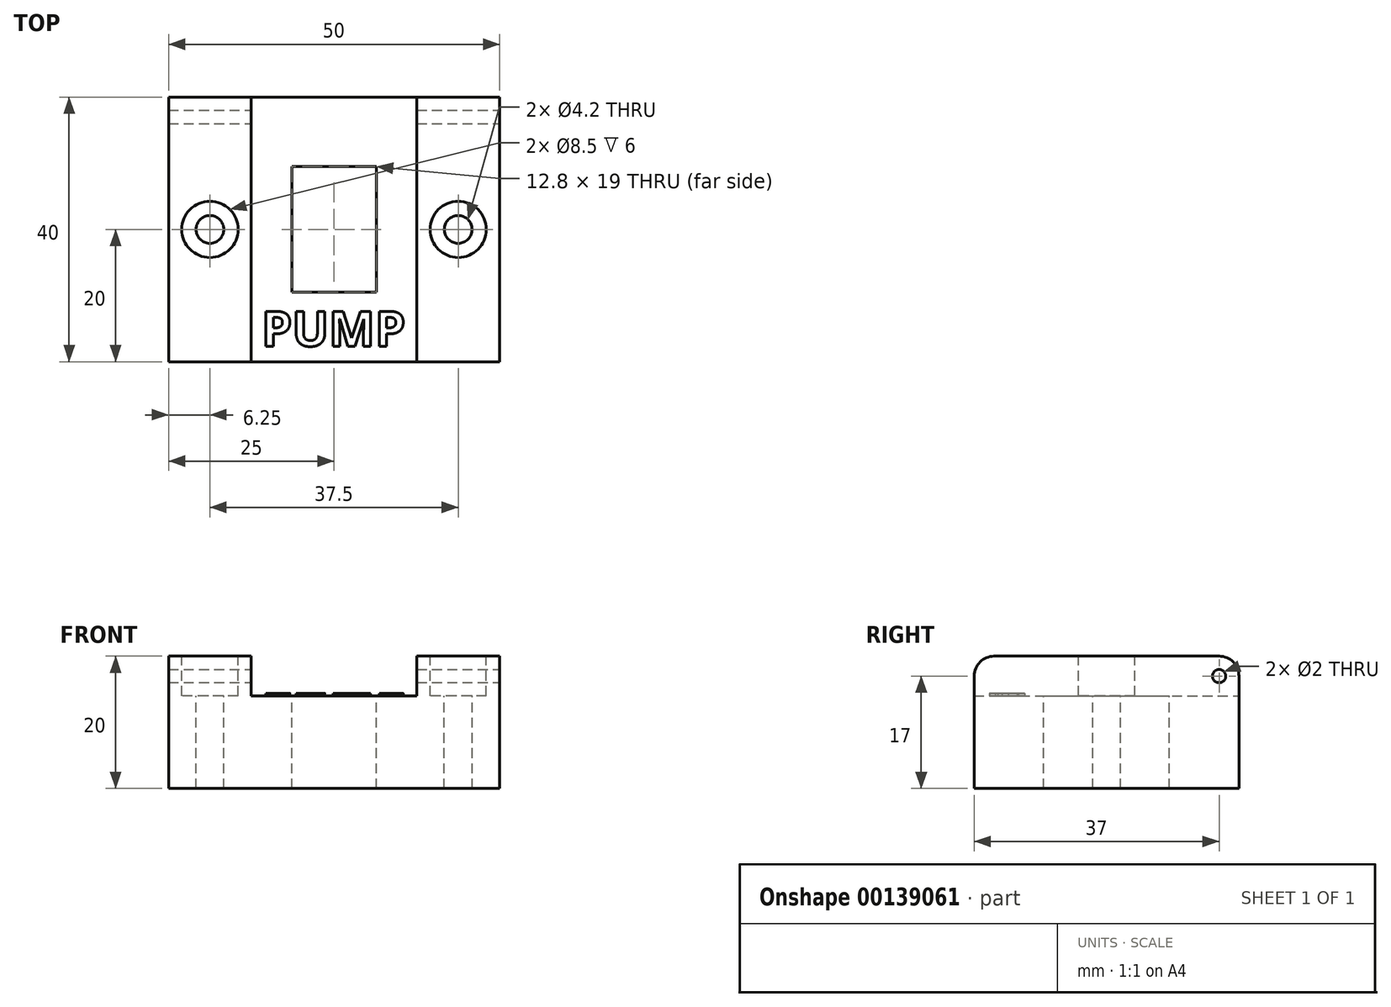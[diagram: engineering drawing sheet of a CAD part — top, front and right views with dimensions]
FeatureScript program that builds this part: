
annotation { "Feature Type Name" : "Feature", "Feature Type Description" : "" }
export const myFeature = defineFeature(function(context is Context, id is Id, definition is map)
    precondition{}
    {
        {
            var Q0;
            Q0=qCreatedBy(makeId("Top.planeOp"),FACE);
            var sketch = newSketch(context, id + "F0", { "sketchPlane" : qUnion([Q0])});
            skLineSegment(sketch, "E0.bottom", {"start": v(25, -20) * mm, "end": v(-25, -20) * mm});
            skLineSegment(sketch, "E0.top", {"start": v(25, 20) * mm, "end": v(-25, 20) * mm});
            skLineSegment(sketch, "E0.left", {"start": v(25, -20) * mm, "end": v(25, 20) * mm});
            skLineSegment(sketch, "E0.right", {"start": v(-25, -20) * mm, "end": v(-25, 20) * mm});
            skPoint(sketch, "E0.middle", {"position": v(0, 0) * mm});
            skSolve(sketch);
        }
        {
            var Q0;
            Q0=makeQuery(id+"F0.imprint","IMPRINT",FACE,{"disambiguationData":[TD([[makeQuery(id+"F0.imprint","IMPRINT",EDGE,{"derivedFrom":sQuery(id+"F0.wireOp",EDGE,"E0.bottom")}),-1.0]])]});
            extrude(context, id + "F1", {"entities" : qUnion([Q0]), "depth" : 14 * mm});
        }
        {
            var Q0;
            Q0=makeQuery(id+"F1.opExtrude","CAP_FACE",FACE,{"disambiguationData":[OSD([sQuery(id+"F0.wireOp",EDGE,"E0.bottom"),sQuery(id+"F0.wireOp",EDGE,"E0.top"),sQuery(id+"F0.wireOp",EDGE,"E0.left"),sQuery(id+"F0.wireOp",EDGE,"E0.right")])],"isStart":false});
            var sketch = newSketch(context, id + "F2", { "sketchPlane" : qUnion([Q0])});
            skLineSegment(sketch, "E1.bottom", {"start": v(6.4, -9.5) * mm, "end": v(-6.4, -9.5) * mm});
            skLineSegment(sketch, "E1.top", {"start": v(6.4, 9.5) * mm, "end": v(-6.4, 9.5) * mm});
            skLineSegment(sketch, "E1.left", {"start": v(6.4, -9.5) * mm, "end": v(6.4, 9.5) * mm});
            skLineSegment(sketch, "E1.right", {"start": v(-6.4, -9.5) * mm, "end": v(-6.4, 9.5) * mm});
            skPoint(sketch, "E1.middle", {"position": v(0, 0) * mm});
            skSolve(sketch);
        }
        {
            var Q0;
            Q0 = qSketchRegion(id + "F2", true);
            extrude(context, id + "F3", {"entities" : qUnion([Q0]), "operationType" : NewBodyOperationType.REMOVE, "endBound" : BoundingType.UP_TO_NEXT, "oppositeDirection" : true, "depth" : 25 * mm});
        }
        {
            var Q0;
            Q0=makeQuery(id+"F1.opExtrude","CAP_FACE",FACE,{"disambiguationData":[OSD([sQuery(id+"F0.wireOp",EDGE,"E0.bottom"),sQuery(id+"F0.wireOp",EDGE,"E0.top"),sQuery(id+"F0.wireOp",EDGE,"E0.left"),sQuery(id+"F0.wireOp",EDGE,"E0.right")])],"isStart":false});
            var sketch = newSketch(context, id + "F4", { "sketchPlane" : qUnion([Q0])});
            skLineSegment(sketch, "E2.bottom", {"start": v(25, -20) * mm, "end": v(-25, -20) * mm});
            skLineSegment(sketch, "E2.top", {"start": v(25, 20) * mm, "end": v(-25, 20) * mm});
            skLineSegment(sketch, "E2.left", {"start": v(25, -20) * mm, "end": v(25, 20) * mm});
            skLineSegment(sketch, "E2.right", {"start": v(-25, -20) * mm, "end": v(-25, 20) * mm});
            skPoint(sketch, "E2.middle", {"position": v(0, 0) * mm});
            skLineSegment(sketch, "E3.bottom", {"start": v(12.5, -20) * mm, "end": v(-12.5, -20) * mm});
            skLineSegment(sketch, "E3.top", {"start": v(12.5, 20) * mm, "end": v(-12.5, 20) * mm});
            skLineSegment(sketch, "E3.left", {"start": v(12.5, -20) * mm, "end": v(12.5, 20) * mm});
            skLineSegment(sketch, "E3.right", {"start": v(-12.5, -20) * mm, "end": v(-12.5, 20) * mm});
            skSolve(sketch);
        }
        {
            var Q0;
            {var subQ0=sQuery(id+"F4.wireOp",EDGE,"E2.right");Q0=makeQuery(id+"F4.imprint","IMPRINT",FACE,{"disambiguationData":[TD([[makeQuery(id+"F4.imprint","IMPRINT",EDGE,{"derivedFrom":subQ0}),-1.0]])]});}
            var Q1;
            {var subQ0=sQuery(id+"F4.wireOp",EDGE,"E2.left");Q1=makeQuery(id+"F4.imprint","IMPRINT",FACE,{"disambiguationData":[TD([[makeQuery(id+"F4.imprint","IMPRINT",EDGE,{"derivedFrom":subQ0}),1.0]])]});}
            extrude(context, id + "F5", {"entities" : qUnion([Q0, Q1]), "operationType" : NewBodyOperationType.ADD, "depth" : 6 * mm});
        }
        {
            var Q0;
            Q0=makeQuery(id+"F5.opExtrude","CAP_FACE",FACE,{"disambiguationData":[OSD([sQuery(id+"F4.wireOp",EDGE,"E2.bottom"),sQuery(id+"F4.wireOp",EDGE,"E2.top"),sQuery(id+"F4.wireOp",EDGE,"E2.left"),sQuery(id+"F4.wireOp",EDGE,"E3.left")])],"isStart":false});
            var sketch = newSketch(context, id + "F6", { "sketchPlane" : qUnion([Q0])});
            skLineSegment(sketch, "E4", {"start": v(-25.03, 0) * mm, "end": v(25, 0) * mm, "construction": true});
            skCircle(sketch, "E5", {"center": v(-18.75, 0) * mm, "radius": 2.1 * mm});
            skCircle(sketch, "E6", {"center": v(18.75, 0) * mm, "radius": 2.1 * mm});
            skSolve(sketch);
        }
        {
            var Q0;
            Q0=makeQuery(id+"F6.imprint","IMPRINT",FACE,{"disambiguationData":[TD([[makeQuery(id+"F6.imprint","IMPRINT",EDGE,{"derivedFrom":sQuery(id+"F6.wireOp",EDGE,"E5")}),1.0]])]});
            var Q1;
            Q1=makeQuery(id+"F6.imprint","IMPRINT",FACE,{"disambiguationData":[TD([[makeQuery(id+"F6.imprint","IMPRINT",EDGE,{"derivedFrom":sQuery(id+"F6.wireOp",EDGE,"E6")}),1.0]])]});
            extrude(context, id + "F7", {"entities" : qUnion([Q0, Q1]), "operationType" : NewBodyOperationType.REMOVE, "endBound" : BoundingType.UP_TO_NEXT, "oppositeDirection" : true, "depth" : 25 * mm});
        }
        {
            var Q0;
            Q0=makeQuery(id+"F5.opExtrude","CAP_FACE",FACE,{"disambiguationData":[OSD([sQuery(id+"F4.wireOp",EDGE,"E2.bottom"),sQuery(id+"F4.wireOp",EDGE,"E2.top"),sQuery(id+"F4.wireOp",EDGE,"E2.right"),sQuery(id+"F4.wireOp",EDGE,"E3.right")])],"isStart":false});
            var sketch = newSketch(context, id + "F8", { "sketchPlane" : qUnion([Q0])});
            skCircle(sketch, "E7", {"center": v(-18.75, 0) * mm, "radius": 4.25 * mm});
            skSolve(sketch);
        }
        {
            var Q0;
            Q0=makeQuery(id+"F8.imprint","IMPRINT",FACE,{"disambiguationData":[TD([[makeQuery(id+"F8.imprint","IMPRINT",EDGE,{"derivedFrom":sQuery(id+"F8.wireOp",EDGE,"E7")}),1.0]])]});
            extrude(context, id + "F9", {"entities" : qUnion([Q0]), "operationType" : NewBodyOperationType.REMOVE, "oppositeDirection" : true, "depth" : 6 * mm});
        }
        {
            var Q0;
            Q0=makeQuery(id+"F5.opExtrude","CAP_FACE",FACE,{"disambiguationData":[OSD([sQuery(id+"F4.wireOp",EDGE,"E2.bottom"),sQuery(id+"F4.wireOp",EDGE,"E2.top"),sQuery(id+"F4.wireOp",EDGE,"E2.left"),sQuery(id+"F4.wireOp",EDGE,"E3.left")])],"isStart":false});
            var sketch = newSketch(context, id + "F10", { "sketchPlane" : qUnion([Q0])});
            skCircle(sketch, "E8", {"center": v(18.75, 0) * mm, "radius": 4.25 * mm});
            skSolve(sketch);
        }
        {
            var Q0;
            Q0 = qSketchRegion(id + "F10", true);
            extrude(context, id + "F11", {"entities" : qUnion([Q0]), "operationType" : NewBodyOperationType.REMOVE, "oppositeDirection" : true, "depth" : 6 * mm});
        }
        {
            var Q0;
            Q0=makeQuery(id+"F5.boolean.opBoolean","MERGE",FACE,{"derivedFrom":[makeQuery(id+"F1.opExtrude","SWEPT_FACE",FACE,{"disambiguationData":[OSD([sQuery(id+"F0.wireOp",EDGE,"E0.left")])]}),makeQuery(id+"F5.opExtrude","SWEPT_FACE",FACE,{"disambiguationData":[OSD([sQuery(id+"F4.wireOp",EDGE,"E2.left")])]})]});
            var sketch = newSketch(context, id + "F12", { "sketchPlane" : qUnion([Q0])});
            skLineSegment(sketch, "E9.bottom", {"start": v(20, 20) * mm, "end": v(14, 20) * mm, "construction": true});
            skLineSegment(sketch, "E9.top", {"start": v(20, 14) * mm, "end": v(14, 14) * mm, "construction": true});
            skLineSegment(sketch, "E9.left", {"start": v(20, 20) * mm, "end": v(20, 14) * mm, "construction": true});
            skLineSegment(sketch, "E9.right", {"start": v(14, 20) * mm, "end": v(14, 14) * mm, "construction": true});
            skLineSegment(sketch, "E10", {"start": v(17, 20) * mm, "end": v(17, 14) * mm, "construction": true});
            skLineSegment(sketch, "E11", {"start": v(20, 17) * mm, "end": v(14, 17) * mm, "construction": true});
            skCircle(sketch, "E12", {"center": v(17, 17) * mm, "radius": 1 * mm});
            skSolve(sketch);
        }
        {
            var Q0;
            Q0=makeQuery(id+"F12.imprint","IMPRINT",FACE,{"disambiguationData":[TD([[makeQuery(id+"F12.imprint","IMPRINT",EDGE,{"derivedFrom":sQuery(id+"F12.wireOp",EDGE,"E12")}),1.0]])]});
            var Q1;
            Q1=sQuery(id+"F12.wireOp",EDGE,"E12");
            extrude(context, id + "F13", {"entities" : qUnion([Q0]), "operationType" : NewBodyOperationType.REMOVE, "surfaceEntities" : qUnion([Q1]), "endBound" : BoundingType.THROUGH_ALL, "oppositeDirection" : true, "depth" : 25 * mm});
        }
        {
            var Q0;
            {var subQ0=sQuery(id+"F4.wireOp",EDGE,"E2.top");Q0=makeQuery(id+"F5.opExtrude","CAP_EDGE",EDGE,{"disambiguationData":[OSD([subQ0]),TDD([makeQuery(id+"F4.imprint","IMPRINT",EDGE,{"disambiguationData":[TD([[makeQuery(id+"F4.imprint","INTERSECT",VERTEX,{"derivedFrom":[subQ0,sQuery(id+"F4.wireOp",EDGE,"E2.left")]}),-1.0]])],"derivedFrom":subQ0})])],"isStart":false});}
            var Q1;
            {var subQ0=sQuery(id+"F4.wireOp",EDGE,"E2.top");Q1=makeQuery(id+"F5.opExtrude","CAP_EDGE",EDGE,{"disambiguationData":[OSD([subQ0]),TDD([makeQuery(id+"F4.imprint","IMPRINT",EDGE,{"disambiguationData":[TD([[makeQuery(id+"F4.imprint","INTERSECT",VERTEX,{"derivedFrom":[subQ0,sQuery(id+"F4.wireOp",EDGE,"E2.right")]}),1.0]])],"derivedFrom":subQ0})])],"isStart":false});}
            var Q2;
            {var subQ0=sQuery(id+"F4.wireOp",EDGE,"E2.bottom");Q2=makeQuery(id+"F5.opExtrude","CAP_EDGE",EDGE,{"disambiguationData":[OSD([subQ0]),TDD([makeQuery(id+"F4.imprint","IMPRINT",EDGE,{"disambiguationData":[TD([[makeQuery(id+"F4.imprint","INTERSECT",VERTEX,{"derivedFrom":[subQ0,sQuery(id+"F4.wireOp",EDGE,"E2.right")]}),1.0]])],"derivedFrom":subQ0})])],"isStart":false});}
            var Q3;
            {var subQ0=sQuery(id+"F4.wireOp",EDGE,"E2.bottom");Q3=makeQuery(id+"F5.opExtrude","CAP_EDGE",EDGE,{"disambiguationData":[OSD([subQ0]),TDD([makeQuery(id+"F4.imprint","IMPRINT",EDGE,{"disambiguationData":[TD([[makeQuery(id+"F4.imprint","INTERSECT",VERTEX,{"derivedFrom":[subQ0,sQuery(id+"F4.wireOp",EDGE,"E2.left")]}),-1.0]])],"derivedFrom":subQ0})])],"isStart":false});}
            fillet(context, id + "F14", {"entities" : qUnion([Q0, Q1, Q2, Q3]), "radius" : 3 * mm, "tangentPropagation" : true, "allowEdgeOverflow" : false});
        }
        {
            var Q0;
            Q0=makeQuery(id+"F1.opExtrude","CAP_FACE",FACE,{"disambiguationData":[OSD([sQuery(id+"F0.wireOp",EDGE,"E0.bottom"),sQuery(id+"F0.wireOp",EDGE,"E0.top"),sQuery(id+"F0.wireOp",EDGE,"E0.left"),sQuery(id+"F0.wireOp",EDGE,"E0.right")])],"isStart":false});
            var sketch = newSketch(context, id + "F15", { "sketchPlane" : qUnion([Q0])});
            skText(sketch, "E13", { "text": "PUMP", "fontName": "OpenSans-Bold.ttf"});
            const initialGuessF15  = {"E13": [-0.01097, -0.01765, 1, 0, 0.0053]};
            skSetInitialGuess(sketch, initialGuessF15);
            skSolve(sketch);
        }
        {
            var Q0;
            Q0 = qSketchRegion(id + "F15", true);
            extrude(context, id + "F16", {"entities" : qUnion([Q0]), "operationType" : NewBodyOperationType.ADD, "depth" : 0.4 * mm});
        }
    });
